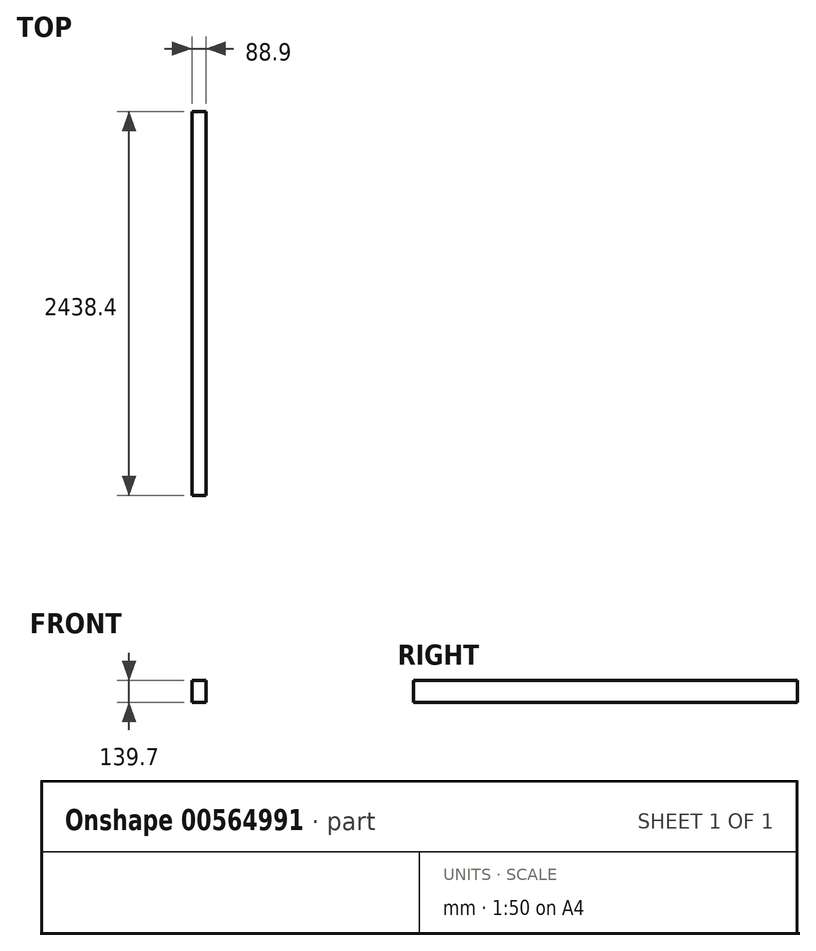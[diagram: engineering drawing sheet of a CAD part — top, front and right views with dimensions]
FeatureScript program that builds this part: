
annotation { "Feature Type Name" : "Feature", "Feature Type Description" : "" }
export const myFeature = defineFeature(function(context is Context, id is Id, definition is map)
    precondition{}
    {
        {
            var Q0;
            Q0=qCreatedBy(makeId("Front.planeOp"),FACE);
            var sketch = newSketch(context, id + "F0", { "sketchPlane" : qUnion([Q0])});
            skLineSegment(sketch, "E0.bottom", {"start": v(0, 0) * mm, "end": v(88.9, 0) * mm});
            skLineSegment(sketch, "E0.top", {"start": v(0, 139.7) * mm, "end": v(88.9, 139.7) * mm});
            skLineSegment(sketch, "E0.left", {"start": v(0, 0) * mm, "end": v(0, 139.7) * mm});
            skLineSegment(sketch, "E0.right", {"start": v(88.9, 0) * mm, "end": v(88.9, 139.7) * mm});
            skSolve(sketch);
        }
        {
            var Q0;
            Q0 = qSketchRegion(id + "F0", true);
            extrude(context, id + "F1", {"entities" : qUnion([Q0]), "depth" : 2438.4 * mm, "offsetDistance" : 25.4 * mm});
        }
    });
